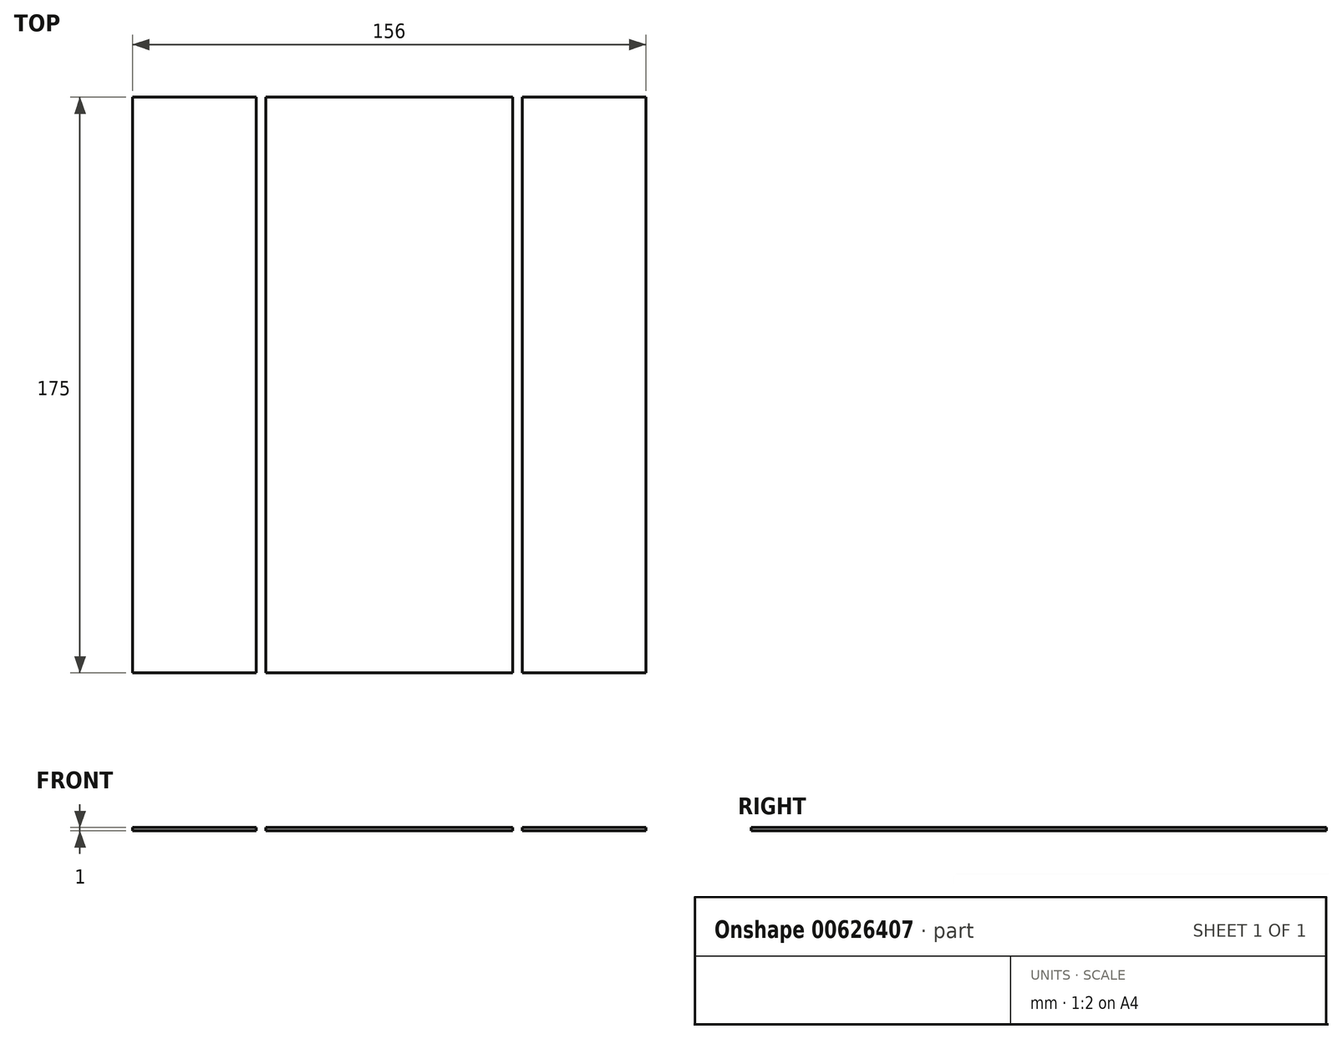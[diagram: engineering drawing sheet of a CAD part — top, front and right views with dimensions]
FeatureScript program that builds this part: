
annotation { "Feature Type Name" : "Feature", "Feature Type Description" : "" }
export const myFeature = defineFeature(function(context is Context, id is Id, definition is map)
    precondition{}
    {
        {
            var Q0;
            Q0=qCreatedBy(makeId("Top.planeOp"),FACE);
            var sketch = newSketch(context, id + "F0", { "sketchPlane" : qUnion([Q0])});
            skLineSegment(sketch, "E0.left", {"start": v(0, 0) * mm, "end": v(0, 175) * mm});
            skLineSegment(sketch, "E0.right", {"start": v(156, 0) * mm, "end": v(156, 175) * mm});
            skLineSegment(sketch, "E1", {"start": v(37.5, 175) * mm, "end": v(37.5, 0) * mm});
            skLineSegment(sketch, "E2", {"start": v(40.5, 175) * mm, "end": v(40.5, 0) * mm});
            skLineSegment(sketch, "E3", {"start": v(115.5, 175) * mm, "end": v(115.5, 0) * mm});
            skLineSegment(sketch, "E4", {"start": v(118.5, 175) * mm, "end": v(118.5, 0) * mm});
            skLineSegment(sketch, "E5", {"start": v(0, 175) * mm, "end": v(37.5, 175) * mm});
            skLineSegment(sketch, "E6", {"start": v(40.5, 175) * mm, "end": v(115.5, 175) * mm});
            skLineSegment(sketch, "E7", {"start": v(118.5, 175) * mm, "end": v(156, 175) * mm});
            skLineSegment(sketch, "E8", {"start": v(156, 0) * mm, "end": v(118.5, 0) * mm});
            skLineSegment(sketch, "E9", {"start": v(115.5, 0) * mm, "end": v(40.5, 0) * mm});
            skLineSegment(sketch, "E10", {"start": v(37.5, 0) * mm, "end": v(0, 0) * mm});
            skSolve(sketch);
        }
        {
            var Q0;
            Q0=makeQuery(id+"F0.imprint","IMPRINT",FACE,{"disambiguationData":[TD([[makeQuery(id+"F0.imprint","IMPRINT",EDGE,{"derivedFrom":sQuery(id+"F0.wireOp",EDGE,"E0.left")}),-1.0]])]});
            var Q1;
            Q1=makeQuery(id+"F0.imprint","IMPRINT",FACE,{"disambiguationData":[TD([[makeQuery(id+"F0.imprint","IMPRINT",EDGE,{"derivedFrom":sQuery(id+"F0.wireOp",EDGE,"E2")}),1.0]])]});
            var Q2;
            Q2=makeQuery(id+"F0.imprint","IMPRINT",FACE,{"disambiguationData":[TD([[makeQuery(id+"F0.imprint","IMPRINT",EDGE,{"derivedFrom":sQuery(id+"F0.wireOp",EDGE,"E0.right")}),1.0]])]});
            extrude(context, id + "F1", {"entities" : qUnion([Q0, Q1, Q2]), "depth" : 1 * mm, "offsetDistance" : 25 * mm});
        }
    });
